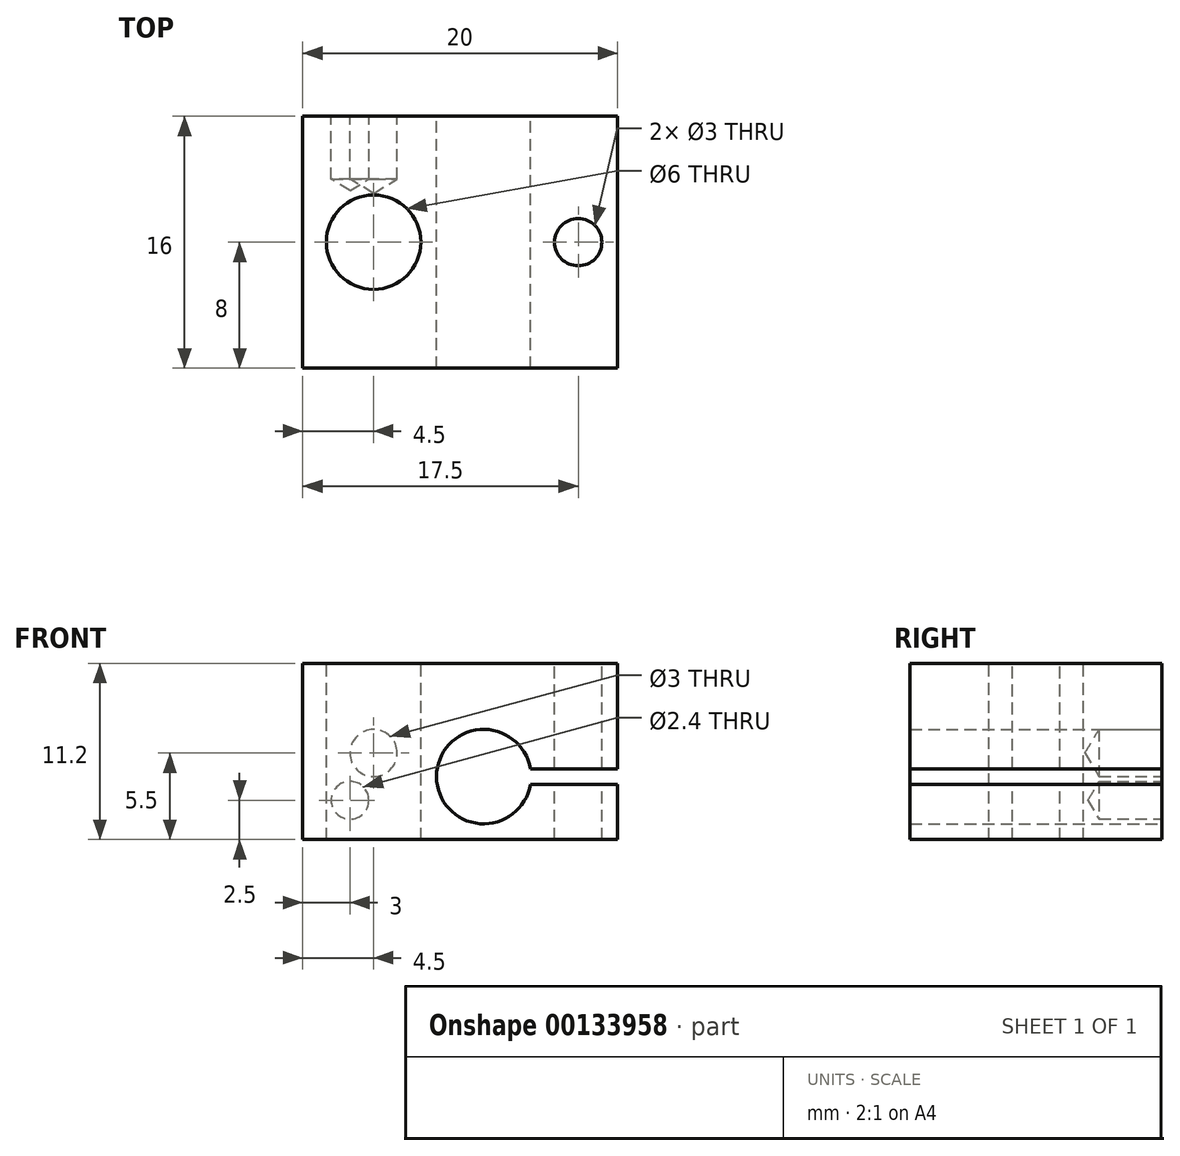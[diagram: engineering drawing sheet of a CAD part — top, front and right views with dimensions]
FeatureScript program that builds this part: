
annotation { "Feature Type Name" : "Feature", "Feature Type Description" : "" }
export const myFeature = defineFeature(function(context is Context, id is Id, definition is map)
    precondition{}
    {
        {
            var Q0;
            Q0=qCreatedBy(makeId("Top.planeOp"),FACE);
            var sketch = newSketch(context, id + "F0", { "sketchPlane" : qUnion([Q0])});
            skLineSegment(sketch, "E0.bottom", {"start": v(10, -8) * mm, "end": v(-10, -8) * mm});
            skLineSegment(sketch, "E0.top", {"start": v(10, 8) * mm, "end": v(-10, 8) * mm});
            skLineSegment(sketch, "E0.left", {"start": v(10, -8) * mm, "end": v(10, 8) * mm});
            skLineSegment(sketch, "E0.right", {"start": v(-10, -8) * mm, "end": v(-10, 8) * mm});
            skPoint(sketch, "E0.middle", {"position": v(0, 0) * mm});
            skSolve(sketch);
        }
        {
            var Q0;
            Q0=makeQuery(id+"F0.imprint","IMPRINT",FACE,{"disambiguationData":[TD([[makeQuery(id+"F0.imprint","IMPRINT",EDGE,{"derivedFrom":sQuery(id+"F0.wireOp",EDGE,"E0.bottom")}),-1.0]])]});
            extrude(context, id + "F1", {"entities" : qUnion([Q0]), "depth" : 11.2 * mm, "offsetDistance" : 25 * mm});
        }
        {
            var Q0;
            Q0=makeQuery(id+"F1.opExtrude","CAP_FACE",FACE,{"disambiguationData":[OSD([sQuery(id+"F0.wireOp",EDGE,"E0.bottom"),sQuery(id+"F0.wireOp",EDGE,"E0.top"),sQuery(id+"F0.wireOp",EDGE,"E0.left"),sQuery(id+"F0.wireOp",EDGE,"E0.right")])],"isStart":false});
            var sketch = newSketch(context, id + "F2", { "sketchPlane" : qUnion([Q0])});
            skPoint(sketch, "E1", {"position": v(-5.5, 0) * mm});
            skPoint(sketch, "E1.positionSnap0", {"position": v(-10, 0) * mm});
            skPoint(sketch, "E2", {"position": v(7.5, 0) * mm});
            skSolve(sketch);
        }
        {
            var Q0;
            Q0=sQuery(id+"F2.wireOp",VERTEX,"E1");
            var Q1;
            Q1=makeQuery(id+"F1.opExtrude","SWEPT_BODY",BODY,{"disambiguationData":[OSD([sQuery(id+"F0.wireOp",EDGE,"E0.bottom"),sQuery(id+"F0.wireOp",EDGE,"E0.top"),sQuery(id+"F0.wireOp",EDGE,"E0.left"),sQuery(id+"F0.wireOp",EDGE,"E0.right")])]});
            hole(context, id + "F3", {"style" : HoleStyle.SIMPLE, "endStyle" : HoleEndStyle.THROUGH, "holeDiameter" : 6 * mm, "majorDiameter" : 5 * mm, "tappedDepth" : 12 * mm, "tapClearance" : 3, "startFromSketch" : true, "locations" : qUnion([Q0]), "scope" : qUnion([Q1])});
        }
        {
            var Q0;
            Q0=sQuery(id+"F2.wireOp",VERTEX,"E2");
            var Q1;
            Q1=makeQuery(id+"F1.opExtrude","SWEPT_BODY",BODY,{"disambiguationData":[OSD([sQuery(id+"F0.wireOp",EDGE,"E0.bottom"),sQuery(id+"F0.wireOp",EDGE,"E0.top"),sQuery(id+"F0.wireOp",EDGE,"E0.left"),sQuery(id+"F0.wireOp",EDGE,"E0.right")])]});
            hole(context, id + "F4", {"style" : HoleStyle.SIMPLE, "endStyle" : HoleEndStyle.THROUGH, "holeDiameter" : 3 * mm, "majorDiameter" : 5 * mm, "tappedDepth" : 12 * mm, "tapClearance" : 3, "startFromSketch" : true, "locations" : qUnion([Q0]), "scope" : qUnion([Q1])});
        }
        {
            var Q0;
            Q0=makeQuery(id+"F1.opExtrude","SWEPT_FACE",FACE,{"disambiguationData":[OSD([sQuery(id+"F0.wireOp",EDGE,"E0.top")])]});
            var sketch = newSketch(context, id + "F5", { "sketchPlane" : qUnion([Q0])});
            skPoint(sketch, "E3", {"position": v(-1.5, 4) * mm});
            skPoint(sketch, "E4", {"position": v(5.5, 5.5) * mm});
            skPoint(sketch, "E5", {"position": v(7, 2.5) * mm});
            skSolve(sketch);
        }
        {
            var Q0;
            Q0=sQuery(id+"F5.wireOp",VERTEX,"E3");
            var Q1;
            Q1=makeQuery(id+"F1.opExtrude","SWEPT_BODY",BODY,{"disambiguationData":[OSD([sQuery(id+"F0.wireOp",EDGE,"E0.bottom"),sQuery(id+"F0.wireOp",EDGE,"E0.top"),sQuery(id+"F0.wireOp",EDGE,"E0.left"),sQuery(id+"F0.wireOp",EDGE,"E0.right")])]});
            hole(context, id + "F6", {"style" : HoleStyle.SIMPLE, "endStyle" : HoleEndStyle.THROUGH, "holeDiameter" : 6 * mm, "majorDiameter" : 5 * mm, "tappedDepth" : 12 * mm, "tapClearance" : 3, "startFromSketch" : true, "locations" : qUnion([Q0]), "scope" : qUnion([Q1])});
        }
        {
            var Q0;
            Q0=sQuery(id+"F5.wireOp",VERTEX,"E4");
            var Q1;
            Q1=makeQuery(id+"F1.opExtrude","SWEPT_BODY",BODY,{"disambiguationData":[OSD([sQuery(id+"F0.wireOp",EDGE,"E0.bottom"),sQuery(id+"F0.wireOp",EDGE,"E0.top"),sQuery(id+"F0.wireOp",EDGE,"E0.left"),sQuery(id+"F0.wireOp",EDGE,"E0.right")])]});
            hole(context, id + "F7", {"style" : HoleStyle.SIMPLE, "endStyle" : HoleEndStyle.BLIND, "holeDiameter" : 3 * mm, "majorDiameter" : 5 * mm, "holeDepth" : 4 * mm, "tappedDepth" : 12 * mm, "tapClearance" : 3, "startFromSketch" : true, "locations" : qUnion([Q0]), "scope" : qUnion([Q1])});
        }
        {
            var Q0;
            Q0=sQuery(id+"F5.wireOp",VERTEX,"E5");
            var Q1;
            Q1=makeQuery(id+"F1.opExtrude","SWEPT_BODY",BODY,{"disambiguationData":[OSD([sQuery(id+"F0.wireOp",EDGE,"E0.bottom"),sQuery(id+"F0.wireOp",EDGE,"E0.top"),sQuery(id+"F0.wireOp",EDGE,"E0.left"),sQuery(id+"F0.wireOp",EDGE,"E0.right")])]});
            hole(context, id + "F8", {"style" : HoleStyle.SIMPLE, "endStyle" : HoleEndStyle.BLIND, "holeDiameter" : 2.4 * mm, "majorDiameter" : 5 * mm, "holeDepth" : 4 * mm, "tappedDepth" : 12 * mm, "tapClearance" : 3, "startFromSketch" : true, "locations" : qUnion([Q0]), "scope" : qUnion([Q1])});
        }
        {
            var Q0;
            {var subQ0=sQuery(id+"F0.wireOp",EDGE,"E0.top");Q0=makeQuery(id+"F5.imprint","IMPRINT",FACE,{"disambiguationData":[TD([[makeQuery(id+"F5.imprint","IMPRINT",EDGE,{"derivedFrom":makeQuery(id+"F1.opExtrude","CAP_EDGE",EDGE,{"disambiguationData":[OSD([subQ0])],"isStart":true})}),1.0]])]});}
            var sketch = newSketch(context, id + "F9", { "sketchPlane" : qUnion([Q0])});
            skLineSegment(sketch, "E6.bottom", {"start": v(-4, 3.5) * mm, "end": v(-16, 3.5) * mm});
            skLineSegment(sketch, "E6.top", {"start": v(-4, 4.5) * mm, "end": v(-16, 4.5) * mm});
            skLineSegment(sketch, "E6.left", {"start": v(-4, 3.5) * mm, "end": v(-4, 4.5) * mm});
            skLineSegment(sketch, "E6.right", {"start": v(-16, 3.5) * mm, "end": v(-16, 4.5) * mm});
            skPoint(sketch, "E6.middle", {"position": v(-10, 4) * mm});
            skSolve(sketch);
        }
        {
            var Q0;
            Q0 = qSketchRegion(id + "F9", true);
            extrude(context, id + "F10", {"entities" : qUnion([Q0]), "operationType" : NewBodyOperationType.REMOVE, "oppositeDirection" : true, "depth" : 25 * mm, "offsetDistance" : 25 * mm});
        }
    });
